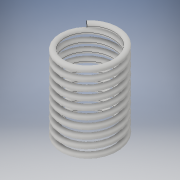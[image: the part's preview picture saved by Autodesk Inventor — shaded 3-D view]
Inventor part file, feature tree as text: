
AUTODESK INVENTOR PART (.ipt)
format: ipt  version: 2018 (Build 220112000, 112)  size: 456,704 bytes
history: native  units: in
note: dims shown in document units (in); Inventor stores cm internally (conversion verified against a paired STEP export)
features: helix x1, sketch x1
ambient origin geometry x8: Origin, YZ Plane, XZ Plane, XY Plane, X Axis, Y Axis, Z Axis, Center Point
bodies: Solid1 (feature_tree)
feature tree (2):
  helix  "Coil1"  [1 undecoded]
  sketch  "Sketch1"  dims[d1=0.1969in d2=1.0in d3=0.5169in d4=3.5433in d5=0.0in d6=90.0deg d7=0.481in d8=90.0deg d9=0.481in]
note: 1 required parameter value undecoded (feature->parameter linkage not recoverable at this tier; creation-order binding heuristic only, values carry confidence <= 0.55)
